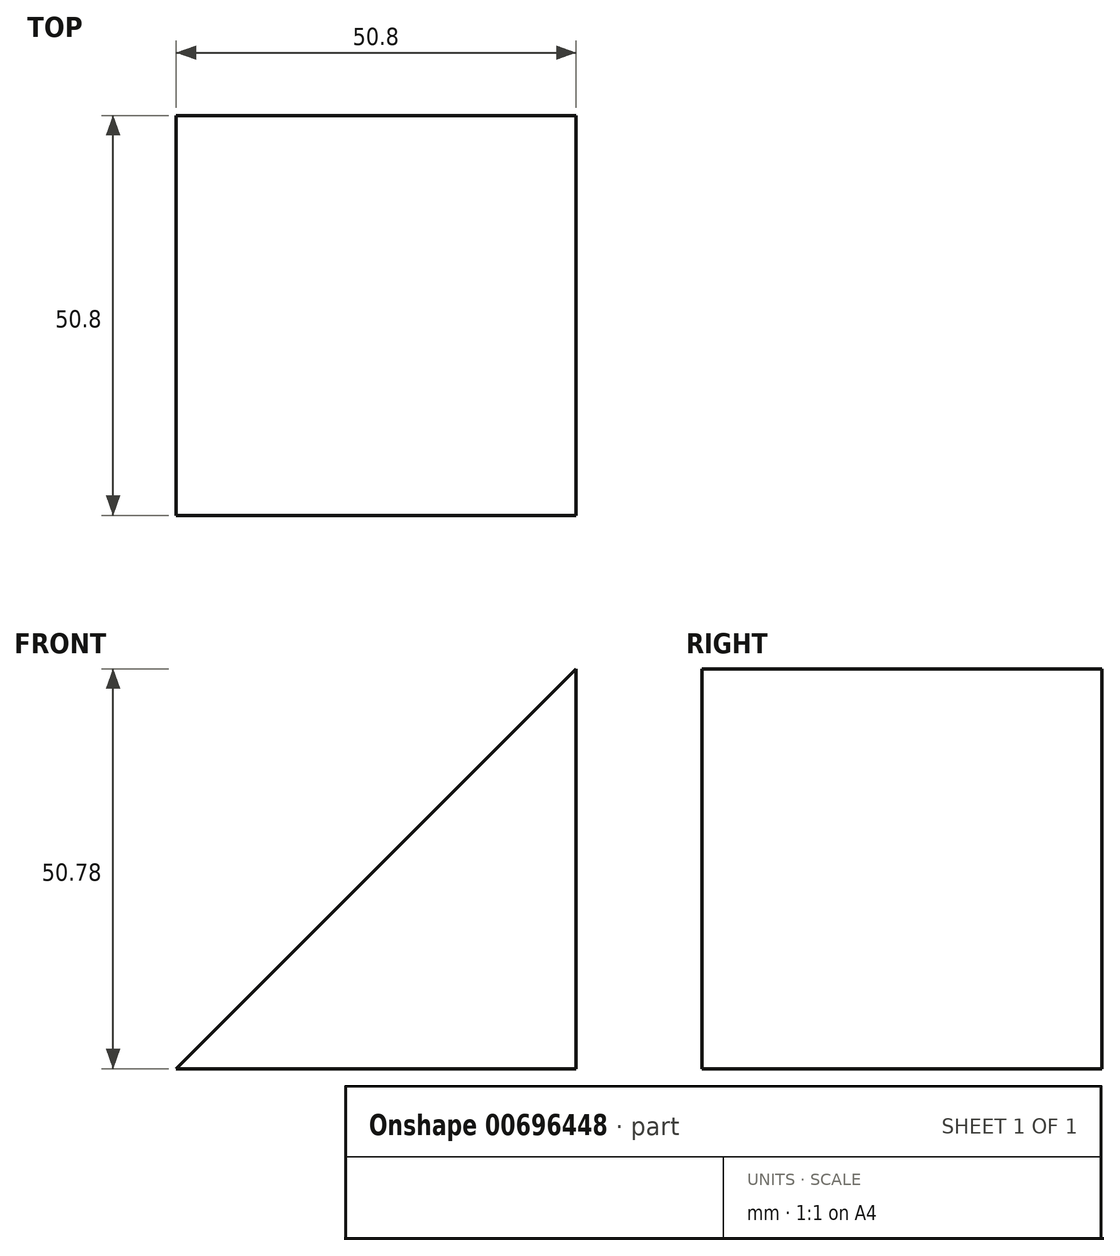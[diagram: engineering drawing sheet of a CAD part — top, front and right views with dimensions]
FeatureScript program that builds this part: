
annotation { "Feature Type Name" : "Feature", "Feature Type Description" : "" }
export const myFeature = defineFeature(function(context is Context, id is Id, definition is map)
    precondition{}
    {
        {
            var Q0;
            Q0=qCreatedBy(makeId("Front.planeOp"),FACE);
            var sketch = newSketch(context, id + "F0", { "sketchPlane" : qUnion([Q0])});
            skLineSegment(sketch, "E0.bottom", {"start": v(0, 0) * mm, "end": v(-50.8, 0) * mm});
            skLineSegment(sketch, "E0.left", {"start": v(0, 0) * mm, "end": v(0, 50.78) * mm});
            skLineSegment(sketch, "E1", {"start": v(-50.8, 0) * mm, "end": v(0, 50.78) * mm});
            skSolve(sketch);
        }
        {
            var Q0;
            Q0=makeQuery(id+"F0.imprint","IMPRINT",FACE,{"disambiguationData":[TD([[makeQuery(id+"F0.imprint","IMPRINT",EDGE,{"derivedFrom":sQuery(id+"F0.wireOp",EDGE,"E0.bottom")}),-1.0]])]});
            extrude(context, id + "F1", {"entities" : qUnion([Q0]), "depth" : 50.8 * mm, "offsetDistance" : 25.4 * mm});
        }
    });
